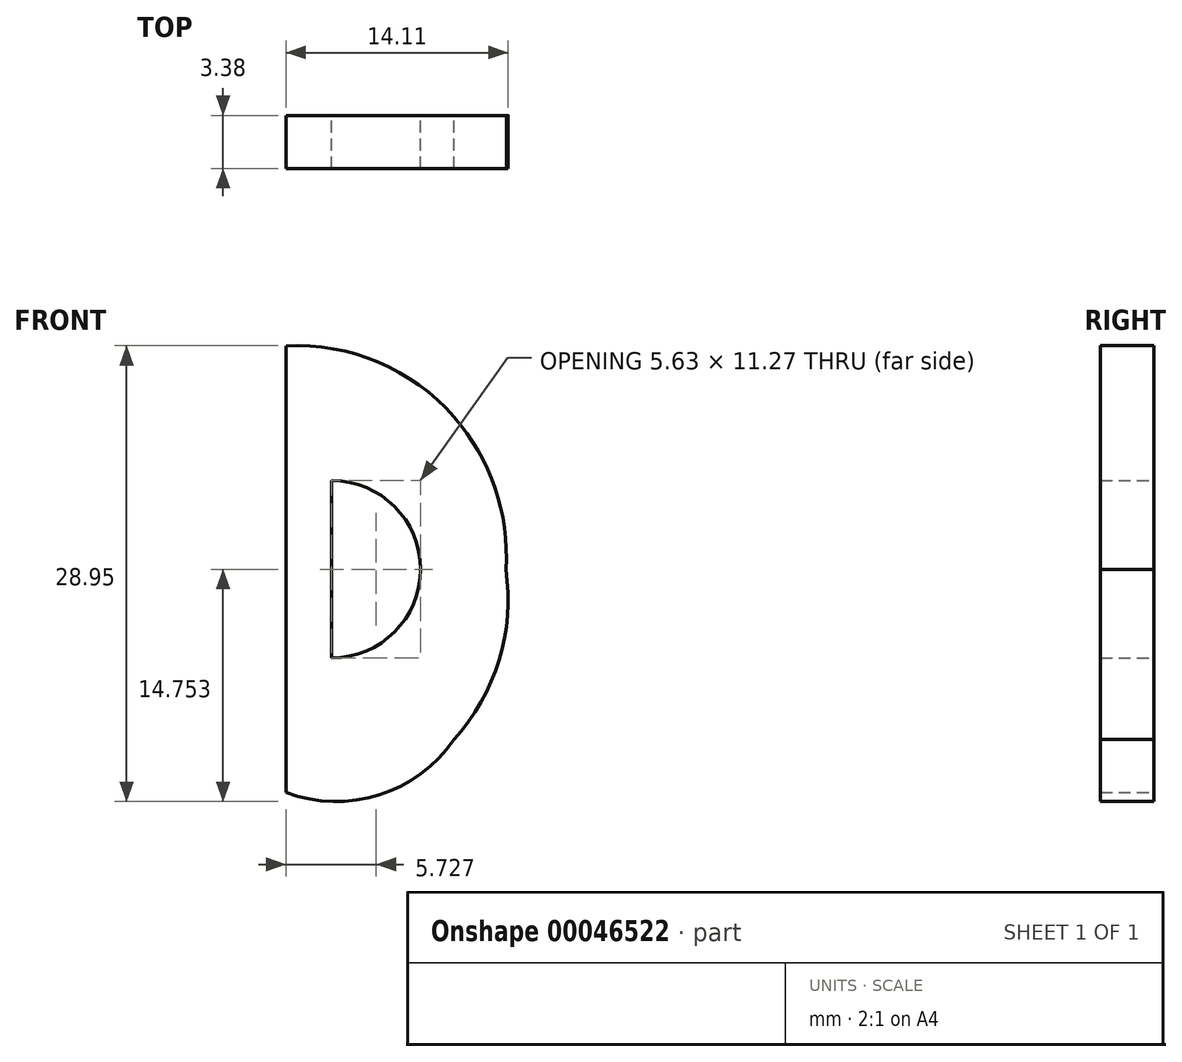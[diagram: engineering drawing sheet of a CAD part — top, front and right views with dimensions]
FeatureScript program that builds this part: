
annotation { "Feature Type Name" : "Feature", "Feature Type Description" : "" }
export const myFeature = defineFeature(function(context is Context, id is Id, definition is map)
    precondition{}
    {
        {
            var Q0;
            Q0=qCreatedBy(makeId("Front.planeOp"),FACE);
            var sketch = newSketch(context, id + "F0", { "sketchPlane" : qUnion([Q0])});
            skLineSegment(sketch, "E0", {"start": v(-1.51, 0) * mm, "end": v(0, 0) * mm});
            skLineSegment(sketch, "E1", {"start": v(4.4, 58.76) * mm, "end": v(4.4, 30.4) * mm});
            skLineSegment(sketch, "E2", {"start": v(7.31, 44.58) * mm, "end": v(7.31, 38.95) * mm});
            skPoint(sketch, "E2.startSnap0", {"position": v(4.4, 44.58) * mm});
            skLineSegment(sketch, "E3", {"start": v(7.31, 44.58) * mm, "end": v(7.31, 50.22) * mm});
            skArc(sketch, "E4", {"start": v(7.31, 50.22) * mm, "mid": v(12.94, 44.58) * mm, "end": v(7.31, 38.95) * mm});
            skArc(sketch, "E5", {"start": v(15.07, 54.26) * mm, "mid": v(10.26, 57.74) * mm, "end": v(4.4, 58.76) * mm});
            skArc(sketch, "E6", {"start": v(18.37, 44.58) * mm, "mid": v(17.68, 49.75) * mm, "end": v(15.07, 54.26) * mm});
            skPoint(sketch, "E6.startSnap0", {"position": v(12.94, 44.58) * mm});
            skArc(sketch, "E7", {"start": v(4.4, 30.4) * mm, "mid": v(10.32, 30.25) * mm, "end": v(15.07, 33.76) * mm});
            skArc(sketch, "E8", {"start": v(15.07, 33.76) * mm, "mid": v(17.93, 38.8) * mm, "end": v(18.37, 44.58) * mm});
            skPoint(sketch, "E9.start.orphan", {"position": v(0, 0) * mm});
            skPoint(sketch, "E10.end.orphan", {"position": v(0, 72.11) * mm});
            skPoint(sketch, "E10.start.orphan", {"position": v(20.97, 72.11) * mm});
            skSolve(sketch);
        }
        {
            var Q0;
            Q0=makeQuery(id+"F0.imprint","IMPRINT",FACE,{"disambiguationData":[TD([[makeQuery(id+"F0.imprint","IMPRINT",EDGE,{"derivedFrom":sQuery(id+"F0.wireOp",EDGE,"E1")}),1.0]])]});
            extrude(context, id + "F1", {"entities" : qUnion([Q0]), "depth" : 3.38 * mm});
        }
    });
